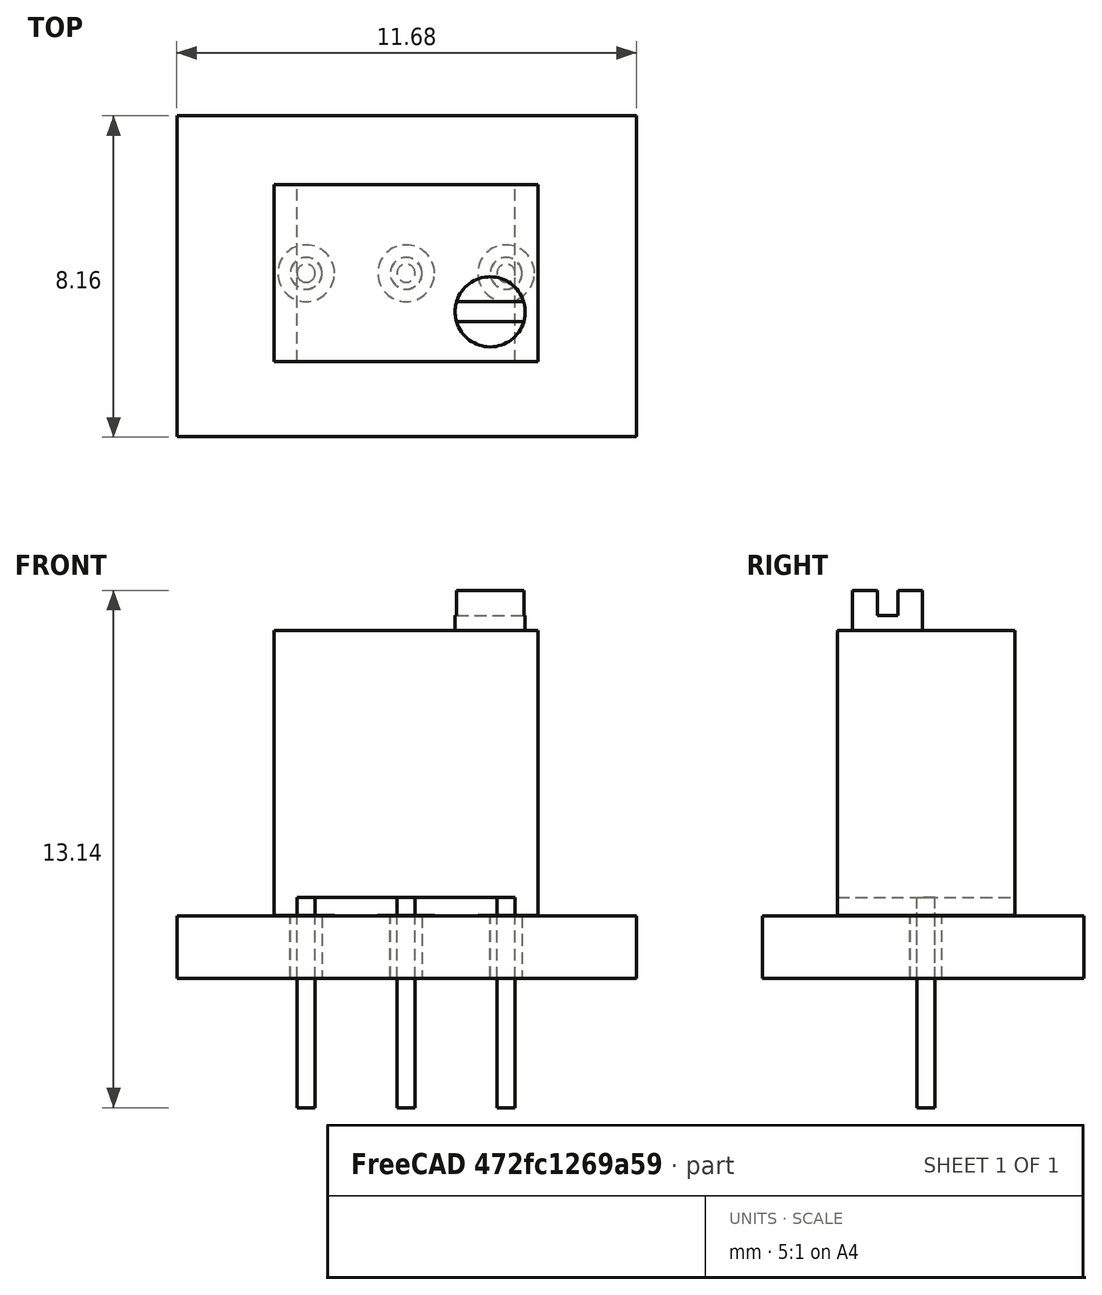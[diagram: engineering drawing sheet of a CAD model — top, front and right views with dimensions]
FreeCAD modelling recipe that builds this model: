
FCSTD DOCUMENT  (FreeCAD 0.18R15611 (Git))
Label: Potentiometer_Bourns_3266Y_Vertical
License: All rights reserved
LicenseURL: http://en.wikipedia.org/wiki/All_rights_reserved
objects: Part::FeaturePython×7, Part::Cylinder×4, Part::Box×4, Part::MultiFuse×2, App::DocumentObjectGroup×1, Part::Cut×1, Part::Feature×1
note: 19 computed .brp shape members not serialized (recipe doc carries the construction recipe); baked Part::Feature solids carry a one-line shape summary decoded from their .brp

FEATURE [Part::FeaturePython] FCrtYd_lines  label="FCrtYd"  # a2plus imported part (geometry in sourceFile) (typed FeaturePython)
  fixedPosition = true
FEATURE [Part::FeaturePython] FFab_lines  label="FFab"  # a2plus imported part (geometry in sourceFile) (typed FeaturePython)
  fixedPosition = true
FEATURE [Part::FeaturePython] Filk_lines  label="FrontSilk"  # a2plus imported part (geometry in sourceFile) (typed FeaturePython)
  fixedPosition = true
FEATURE [Part::FeaturePython] TopPads  # a2plus imported part (geometry in sourceFile) (typed FeaturePython)
  fixedPosition = true
FEATURE [Part::FeaturePython] BotPads  # a2plus imported part (geometry in sourceFile) (typed FeaturePython)
  fixedPosition = true
FEATURE [Part::FeaturePython] THPs  label="PTHs"  # a2plus imported part (geometry in sourceFile) (typed FeaturePython)
  fixedPosition = true
FEATURE [Part::FeaturePython] newPCB  label="Pcb"  # a2plus imported part (geometry in sourceFile) (typed FeaturePython)
  fixedPosition = true
FEATURE [App::DocumentObjectGroup] Potentiometer_Bourns_3266Y_Vertical_fp
  Group = -> [FCrtYd_lines,FFab_lines,Filk_lines,TopPads,BotPads,THPs,newPCB]
FEATURE [Part::Cylinder] Cylinder  label="Pin1"
  Angle = 360
  AttacherType = Attacher::AttachEngine3D
  Height = 5.34
  Placement = pos=(0,0,-4.88) rot=(0,0,1;0rad)
  Radius = 0.23
FEATURE [Part::Cylinder] Cylinder001  label="Pin3"
  Angle = 360
  AttacherType = Attacher::AttachEngine3D
  Height = 5.34
  Placement = pos=(-5.08,0,-4.88) rot=(0,0,1;0rad)
  Radius = 0.23
FEATURE [Part::Cylinder] Cylinder002  label="Pin2"
  Angle = 360
  AttacherType = Attacher::AttachEngine3D
  Height = 5.34
  Placement = pos=(-2.54,0,-4.88) rot=(0,0,1;0rad)
  Radius = 0.23
FEATURE [Part::Box] Box  label="Body"
  AttacherType = Attacher::AttachEngine3D
  Height = 6.78
  Length = 6.71
  Placement = pos=(-5.895,-3.52,0.46) rot=(0,0,1;0rad)
  Width = 4.5
FEATURE [Part::Box] Box001  label="Standoff1"
  AttacherType = Attacher::AttachEngine3D
  Height = 0.46
  Length = 0.585
  Placement = pos=(0.23,-3.52,0) rot=(0,0,1;0rad)
  Width = 4.5
FEATURE [Part::Box] Box002  label="Standoff2"
  AttacherType = Attacher::AttachEngine3D
  Height = 0.46
  Length = 0.585
  Placement = pos=(-5.895,-3.52,0) rot=(0,0,1;0rad)
  Width = 4.5
FEATURE [Part::MultiFuse] Fusion  label="FusionBody"
  Placement = pos=(0,1.27,0) rot=(0,0,1;0rad)
  Refine = true
  Shapes = -> [Box,Box001,Box002]
FEATURE [Part::Cylinder] Cylinder003  label="Knob"
  Angle = 360
  AttacherType = Attacher::AttachEngine3D
  Height = 1.02
  Placement = pos=(-0.405,-2.25,7.24) rot=(0,0,1;0rad)
  Radius = 0.89
FEATURE [Part::Box] Box003  label="Cube"
  AttacherType = Attacher::AttachEngine3D
  Height = 0.64
  Length = 10
  Placement = pos=(-5,-2.5,7.62) rot=(0,0,1;0rad)
  Width = 0.51
FEATURE [Part::Cut] Cut  label="CutKnob"
  Base = -> Cylinder003
  Placement = pos=(0,1.27,0) rot=(0,0,1;0rad)
  Refine = true
  Tool = -> Box003
FEATURE [Part::MultiFuse] Pin1_mp_cp  label="Pin1_fd"
  Refine = true
  Shapes = -> [Cylinder,Cylinder001,Cylinder002,Fusion,Cut]
FEATURE [Part::Feature] Shape  label="Potentiometer_Bourns_3266Y_Vertical"
  shape: bbox 6.71 x 4.5 x 13.14 mm, 22 faces (baked)
